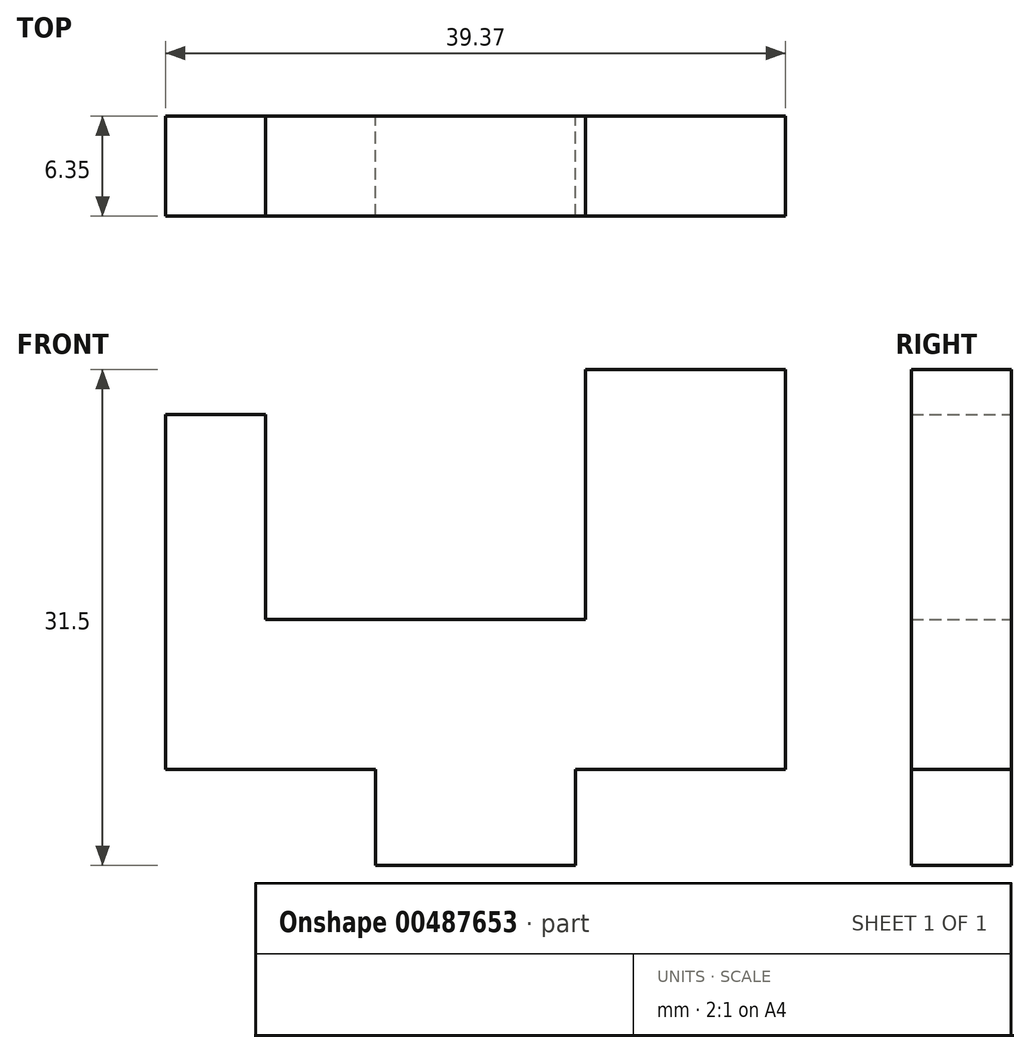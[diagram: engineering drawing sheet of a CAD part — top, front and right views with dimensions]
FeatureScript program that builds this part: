
annotation { "Feature Type Name" : "Feature", "Feature Type Description" : "" }
export const myFeature = defineFeature(function(context is Context, id is Id, definition is map)
    precondition{}
    {
        {
            var Q0;
            Q0=qCreatedBy(makeId("Front.planeOp"),FACE);
            var sketch = newSketch(context, id + "F0", { "sketchPlane" : qUnion([Q0])});
            skLineSegment(sketch, "E0.top", {"start": v(0, 25.4) * mm, "end": v(12.7, 25.4) * mm});
            skLineSegment(sketch, "E0.left", {"start": v(0, 9.53) * mm, "end": v(0, 25.4) * mm});
            skLineSegment(sketch, "E0.right", {"start": v(12.7, 0) * mm, "end": v(12.7, 25.4) * mm});
            skLineSegment(sketch, "E1.bottom", {"start": v(0, 0) * mm, "end": v(-0.64, 0) * mm});
            skLineSegment(sketch, "E1.top", {"start": v(0, 9.53) * mm, "end": v(-20.32, 9.52) * mm});
            skLineSegment(sketch, "E2.top", {"start": v(-20.32, 22.54) * mm, "end": v(-26.67, 22.54) * mm});
            skLineSegment(sketch, "E2.left", {"start": v(-20.32, 9.53) * mm, "end": v(-20.32, 22.54) * mm});
            skLineSegment(sketch, "E2.right", {"start": v(-26.67, 0) * mm, "end": v(-26.67, 22.54) * mm});
            skLineSegment(sketch, "E3.top", {"start": v(-13.34, -6.1) * mm, "end": v(-0.64, -6.1) * mm});
            skLineSegment(sketch, "E3.left", {"start": v(-13.34, 0) * mm, "end": v(-13.34, -6.1) * mm});
            skLineSegment(sketch, "E3.right", {"start": v(-0.64, 0) * mm, "end": v(-0.64, -6.1) * mm});
            skLineSegment(sketch, "E4", {"start": v(-26.67, 0) * mm, "end": v(12.7, 0) * mm});
            skSolve(sketch);
        }
        {
            var Q0;
            Q0 = qSketchRegion(id + "F0", true);
            extrude(context, id + "F1", {"entities" : qUnion([Q0]), "depth" : 6.35 * mm});
        }
    });
